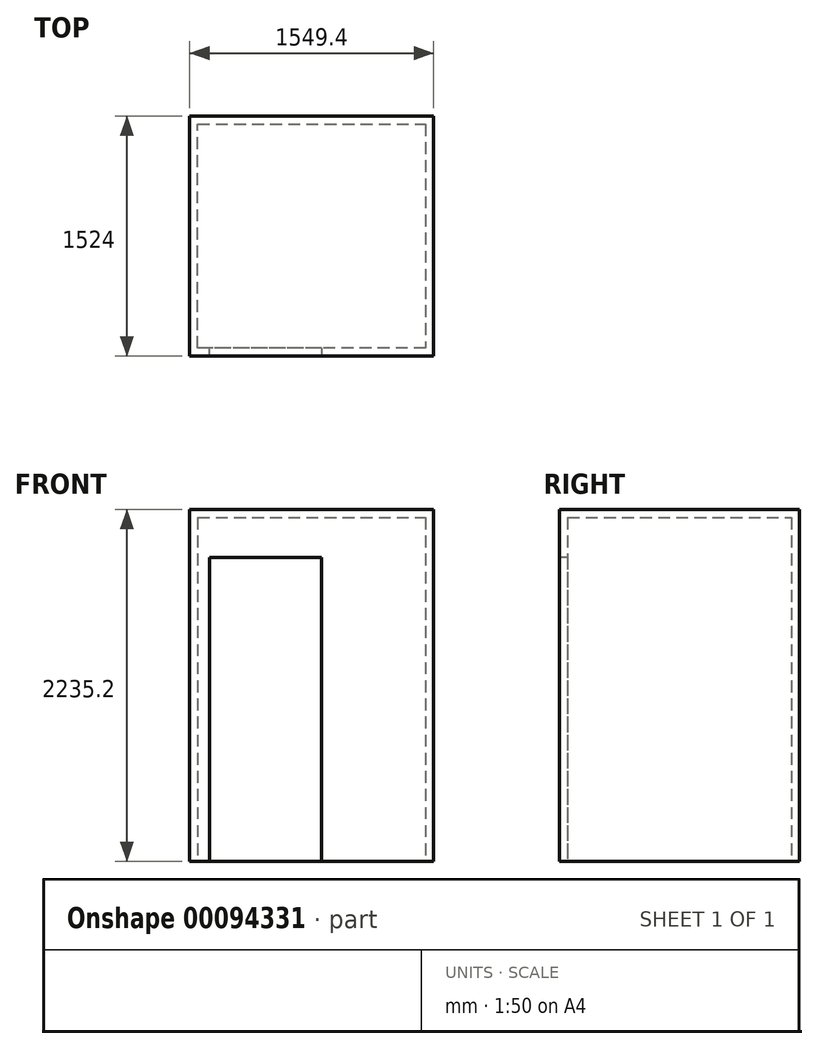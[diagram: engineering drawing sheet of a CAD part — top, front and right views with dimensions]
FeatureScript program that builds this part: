
annotation { "Feature Type Name" : "Feature", "Feature Type Description" : "" }
export const myFeature = defineFeature(function(context is Context, id is Id, definition is map)
    precondition{}
    {
        {
            var Q0;
            Q0=qCreatedBy(makeId("Top.planeOp"),FACE);
            var sketch = newSketch(context, id + "F0", { "sketchPlane" : qUnion([Q0])});
            skLineSegment(sketch, "E0.bottom", {"start": v(0, 0) * mm, "end": v(-1549.4, 0) * mm});
            skLineSegment(sketch, "E0.top", {"start": v(0, -1524) * mm, "end": v(-711.2, -1524) * mm});
            skLineSegment(sketch, "E0.left", {"start": v(0, 0) * mm, "end": v(0, -1524) * mm});
            skLineSegment(sketch, "E0.right", {"start": v(-1549.4, 0) * mm, "end": v(-1549.4, -1524) * mm});
            skLineSegment(sketch, "E1", {"start": v(-1422.4, -1524) * mm, "end": v(-1422.4, -1473.2) * mm});
            skLineSegment(sketch, "E2", {"start": v(-1422.4, -1473.2) * mm, "end": v(-1498.6, -1473.2) * mm});
            skLineSegment(sketch, "E3", {"start": v(-1498.6, -1473.2) * mm, "end": v(-1498.6, -50.8) * mm});
            skLineSegment(sketch, "E4", {"start": v(-1498.6, -50.8) * mm, "end": v(-50.8, -50.8) * mm});
            skLineSegment(sketch, "E5", {"start": v(-50.8, -50.8) * mm, "end": v(-50.8, -1473.2) * mm});
            skLineSegment(sketch, "E6", {"start": v(-50.8, -1473.2) * mm, "end": v(-711.2, -1473.2) * mm});
            skLineSegment(sketch, "E7", {"start": v(-711.2, -1473.2) * mm, "end": v(-711.2, -1524) * mm});
            skLineSegment(sketch, "E8", {"start": v(-50.8, -1473.2) * mm, "end": v(0, -1473.2) * mm, "construction": true});
            skLineSegment(sketch, "E9", {"start": v(-774.7, -50.8) * mm, "end": v(-774.7, 0) * mm, "construction": true});
            skLineSegment(sketch, "E10", {"start": v(-1498.6, -762) * mm, "end": v(-1549.4, -762) * mm, "construction": true});
            skLineSegment(sketch, "E11.trimOffspring", {"start": v(-1422.4, -1524) * mm, "end": v(-1549.4, -1524) * mm});
            skSolve(sketch);
        }
        {
            var Q0;
            Q0=makeQuery(id+"F0.imprint","IMPRINT",FACE,{"disambiguationData":[TD([[makeQuery(id+"F0.imprint","IMPRINT",EDGE,{"derivedFrom":sQuery(id+"F0.wireOp",EDGE,"E0.bottom")}),1.0]])]});
            extrude(context, id + "F1", {"entities" : qUnion([Q0]), "depth" : 1930.4 * mm});
        }
        {
            var Q0;
            Q0=makeQuery(id+"F1.opExtrude","CAP_FACE",FACE,{"disambiguationData":[OSD([sQuery(id+"F0.wireOp",EDGE,"E0.bottom"),sQuery(id+"F0.wireOp",EDGE,"E0.top"),sQuery(id+"F0.wireOp",EDGE,"E0.left"),sQuery(id+"F0.wireOp",EDGE,"E0.right"),sQuery(id+"F0.wireOp",EDGE,"E1"),sQuery(id+"F0.wireOp",EDGE,"E2"),sQuery(id+"F0.wireOp",EDGE,"E3"),sQuery(id+"F0.wireOp",EDGE,"E4"),sQuery(id+"F0.wireOp",EDGE,"E5"),sQuery(id+"F0.wireOp",EDGE,"E6"),sQuery(id+"F0.wireOp",EDGE,"E7"),sQuery(id+"F0.wireOp",EDGE,"E11.trimOffspring")])],"isStart":false});
            var sketch = newSketch(context, id + "F2", { "sketchPlane" : qUnion([Q0])});
            skLineSegment(sketch, "E12.bottom", {"start": v(-1549.4, 0) * mm, "end": v(0, 0) * mm});
            skLineSegment(sketch, "E12.top", {"start": v(-1549.4, -1524) * mm, "end": v(0, -1524) * mm});
            skLineSegment(sketch, "E12.left", {"start": v(-1549.4, 0) * mm, "end": v(-1549.4, -1524) * mm});
            skLineSegment(sketch, "E12.right", {"start": v(0, 0) * mm, "end": v(0, -1524) * mm});
            skSolve(sketch);
        }
        {
            var Q0;
            Q0 = qSketchRegion(id + "F2", true);
            extrude(context, id + "F3", {"entities" : qUnion([Q0]), "operationType" : NewBodyOperationType.ADD, "depth" : 304.8 * mm});
        }
        {
            var Q0;
            Q0=makeQuery(id+"F3.opExtrude","CAP_FACE",FACE,{"disambiguationData":[OSD([sQuery(id+"F2.wireOp",EDGE,"E12.bottom"),sQuery(id+"F2.wireOp",EDGE,"E12.top"),sQuery(id+"F2.wireOp",EDGE,"E12.left"),sQuery(id+"F2.wireOp",EDGE,"E12.right")])],"isStart":true});
            var sketch = newSketch(context, id + "F4", { "sketchPlane" : qUnion([Q0])});
            skLineSegment(sketch, "E13.bottom", {"start": v(-50.8, 50.8) * mm, "end": v(-1498.6, 50.8) * mm});
            skLineSegment(sketch, "E13.top", {"start": v(-50.8, 1473.2) * mm, "end": v(-1498.6, 1473.2) * mm});
            skLineSegment(sketch, "E13.left", {"start": v(-50.8, 50.8) * mm, "end": v(-50.8, 1473.2) * mm});
            skLineSegment(sketch, "E13.right", {"start": v(-1498.6, 50.8) * mm, "end": v(-1498.6, 1473.2) * mm});
            skSolve(sketch);
        }
        {
            var Q0;
            Q0 = qSketchRegion(id + "F4", true);
            extrude(context, id + "F5", {"entities" : qUnion([Q0]), "operationType" : NewBodyOperationType.REMOVE, "oppositeDirection" : true, "depth" : 254 * mm});
        }
    });
